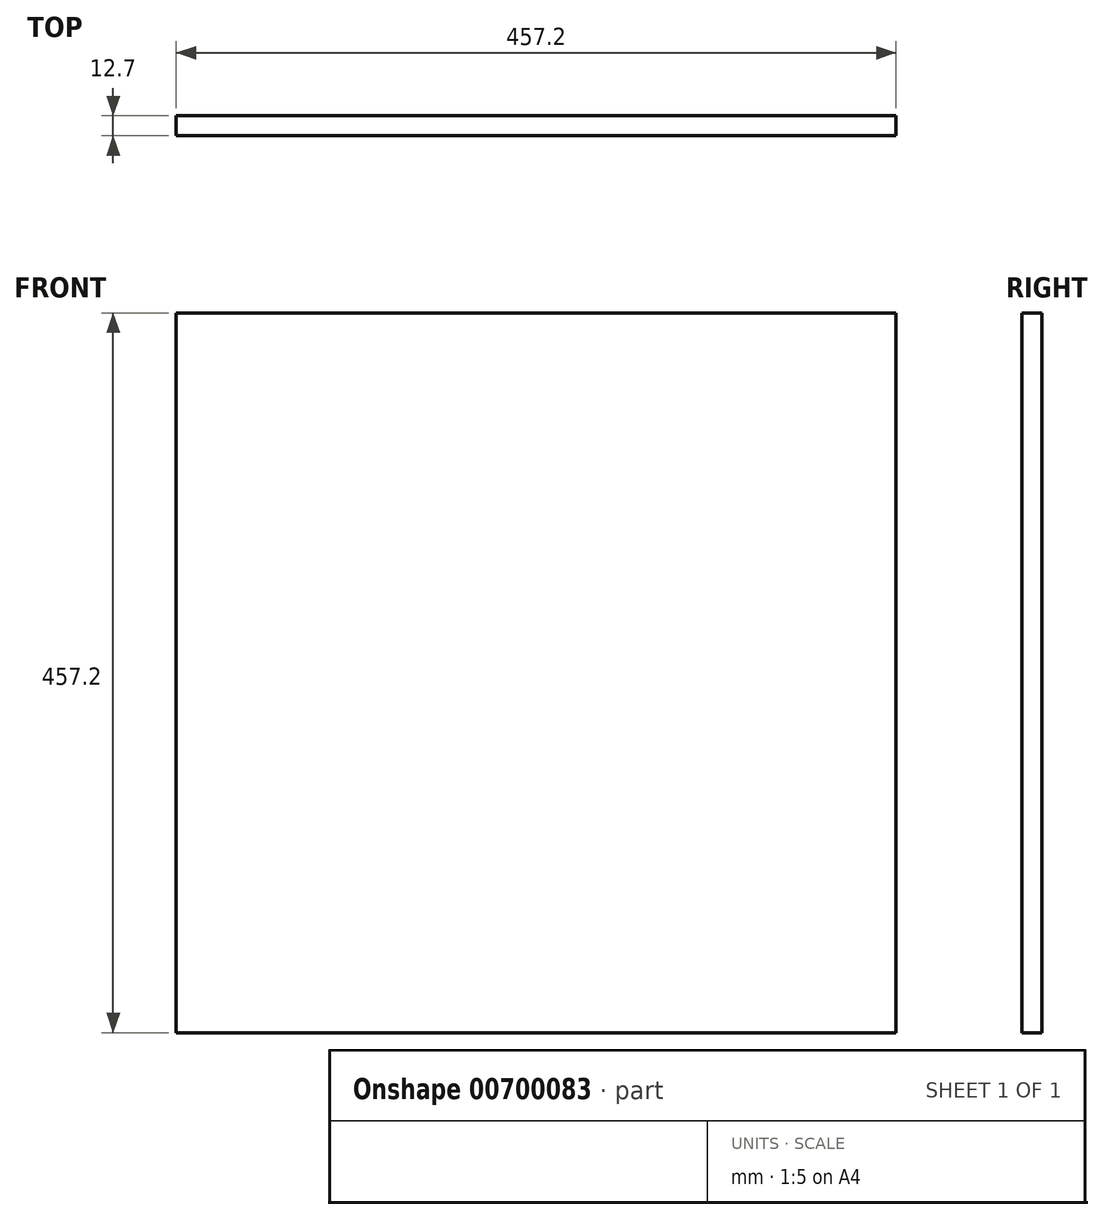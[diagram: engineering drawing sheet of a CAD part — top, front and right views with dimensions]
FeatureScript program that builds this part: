
annotation { "Feature Type Name" : "Feature", "Feature Type Description" : "" }
export const myFeature = defineFeature(function(context is Context, id is Id, definition is map)
    precondition{}
    {
        {
            var Q0;
            Q0=qCreatedBy(makeId("Top.planeOp"),FACE);
            var sketch = newSketch(context, id + "F0", { "sketchPlane" : qUnion([Q0])});
            skLineSegment(sketch, "E0.bottom", {"start": v(228.6, -6.35) * mm, "end": v(-228.6, -6.35) * mm});
            skLineSegment(sketch, "E0.top", {"start": v(228.6, 6.35) * mm, "end": v(-228.6, 6.35) * mm});
            skLineSegment(sketch, "E0.left", {"start": v(228.6, -6.35) * mm, "end": v(228.6, 6.35) * mm});
            skLineSegment(sketch, "E0.right", {"start": v(-228.6, -6.35) * mm, "end": v(-228.6, 6.35) * mm});
            skPoint(sketch, "E0.middle", {"position": v(0, 0) * mm});
            skSolve(sketch);
        }
        {
            var Q0;
            Q0 = qSketchRegion(id + "F0", true);
            var Q1;
            Q1=makeQuery(id+"F0.imprint","IMPRINT",FACE,{"disambiguationData":[TD([[makeQuery(id+"F0.imprint","IMPRINT",EDGE,{"derivedFrom":sQuery(id+"F0.wireOp",EDGE,"E0.bottom")}),-1.0]])]});
            extrude(context, id + "F1", {"entities" : qUnion([Q0, Q1]), "depth" : 457.2 * mm, "offsetDistance" : 25.4 * mm});
        }
    });
